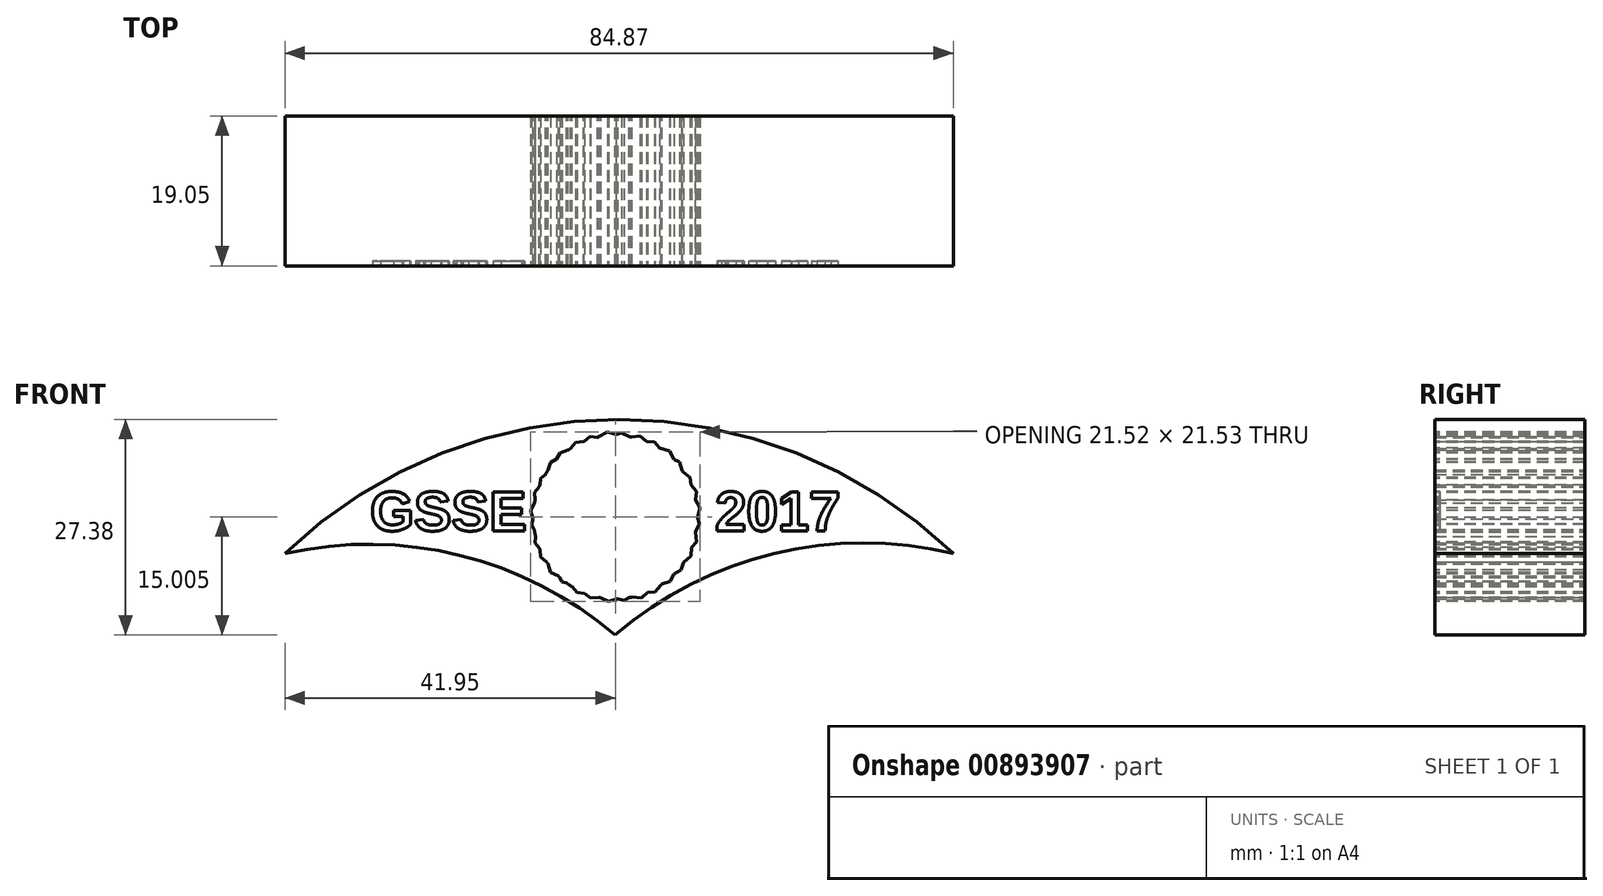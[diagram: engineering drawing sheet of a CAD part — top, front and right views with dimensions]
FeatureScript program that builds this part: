
annotation { "Feature Type Name" : "Feature", "Feature Type Description" : "" }
export const myFeature = defineFeature(function(context is Context, id is Id, definition is map)
    precondition{}
    {
        {
            var Q0;
            Q0=qCreatedBy(makeId("Front.planeOp"),FACE);
            var sketch = newSketch(context, id + "F0", { "sketchPlane" : qUnion([Q0])});
            skArc(sketch, "E0", {"start": v(0, 0) * mm, "mid": v(-19.73, 10.13) * mm, "end": v(-41.91, 10.32) * mm});
            skArc(sketch, "E1", {"start": v(42.96, 10.33) * mm, "mid": v(20.23, 10.36) * mm, "end": v(0, 0) * mm});
            skArc(sketch, "E2", {"start": v(42.96, 10.33) * mm, "mid": v(0.52, 27.38) * mm, "end": v(-41.91, 10.32) * mm});
            skCircle(sketch, "E3", {"center": v(0, 14.96) * mm, "radius": 10.39 * mm});
            skLineSegment(sketch, "E4", {"start": v(42.96, 10.33) * mm, "end": v(0, 10.33) * mm, "construction": true});
            skLineSegment(sketch, "E5", {"start": v(0, 10.33) * mm, "end": v(-41.91, 10.33) * mm, "construction": true});
            skLineSegment(sketch, "E6", {"start": v(10.39, 14.96) * mm, "end": v(-10.39, 14.96) * mm, "construction": true});
            skLineSegment(sketch, "E7", {"start": v(0, 0) * mm, "end": v(0, 27.38) * mm, "construction": true});
            skSolve(sketch);
        }
        {
            var Q0;
            Q0=makeQuery(id+"F0.imprint","IMPRINT",FACE,{"disambiguationData":[TD([[makeQuery(id+"F0.imprint","IMPRINT",EDGE,{"derivedFrom":sQuery(id+"F0.wireOp",EDGE,"E0")}),-1.0]])]});
            extrude(context, id + "F1", {"entities" : qUnion([Q0]), "depth" : 19.05 * mm, "offsetDistance" : 25.4 * mm});
        }
        {
            var Q0;
            Q0=makeQuery(id+"F1.opExtrude","CAP_FACE",FACE,{"disambiguationData":[OSD([sQuery(id+"F0.wireOp",EDGE,"E0"),sQuery(id+"F0.wireOp",EDGE,"E1"),sQuery(id+"F0.wireOp",EDGE,"E2"),sQuery(id+"F0.wireOp",EDGE,"E3")])],"isStart":false});
            var sketch = newSketch(context, id + "F2", { "sketchPlane" : qUnion([Q0])});
            skText(sketch, "E8", { "text": "GSSE", "fontName": "Arimo-Bold.ttf"});
            skLineSegment(sketch, "E9", {"start": v(-31.44, 18.39) * mm, "end": v(32.5, 18.39) * mm, "construction": true});
            skLineSegment(sketch, "E10", {"start": v(-38.65, 13.24) * mm, "end": v(39.7, 13.24) * mm, "construction": true});
            skLineSegment(sketch, "E11", {"start": v(0, 18.39) * mm, "end": v(0, 13.24) * mm, "construction": true});
            skLineSegment(sketch, "E12", {"start": v(-11, 15.81) * mm, "end": v(0, 15.81) * mm, "construction": true});
            skLineSegment(sketch, "E13", {"start": v(0, 15.81) * mm, "end": v(12.72, 16.05) * mm, "construction": true});
            skLineSegment(sketch, "E14", {"start": v(-31.11, 15.81) * mm, "end": v(-35.32, 15.81) * mm, "construction": true});
            skLineSegment(sketch, "E15", {"start": v(32.02, 15.33) * mm, "end": v(28.82, 15.33) * mm, "construction": true});
            skLineSegment(sketch, "E16", {"start": v(28.82, 18.39) * mm, "end": v(28.82, 13.24) * mm, "construction": true});
            skLineSegment(sketch, "E17", {"start": v(12.72, 18.39) * mm, "end": v(12.72, 13.24) * mm, "construction": true});
            skText(sketch, "E18", { "text": "2017", "fontName": "Arimo-Bold.ttf"});
            const initialGuessF2  = {"E8": [-0.03111, 0.01324, 1, 0, 0.00515], "E18": [0.01272, 0.01324, 1, 0, 0.00515]};
            skSetInitialGuess(sketch, initialGuessF2);
            skSolve(sketch);
        }
        {
            var Q0;
            Q0 = qSketchRegion(id + "F2", true);
            extrude(context, id + "F3", {"entities" : qUnion([Q0]), "operationType" : NewBodyOperationType.REMOVE, "oppositeDirection" : true, "depth" : 0.64 * mm, "offsetDistance" : 25.4 * mm});
        }
        {
            var Q0;
            {var subQ0=sQuery(id+"F0.wireOp",EDGE,"E1");var subQ1=sQuery(id+"F0.wireOp",EDGE,"E3");var subQ2=sQuery(id+"F0.wireOp",EDGE,"E0");var subQ3=sQuery(id+"F0.wireOp",EDGE,"E2");Q0=makeQuery(id+"F3.boolean.opBoolean","SPLIT",FACE,{"disambiguationData":[TD([makeQuery(id+"F1.opExtrude","SWEPT_FACE",FACE,{"disambiguationData":[OSD([subQ2])]})])],"derivedFrom":makeQuery(id+"F1.opExtrude","CAP_FACE",FACE,{"disambiguationData":[OSD([subQ2,subQ0,subQ3,subQ1])],"isStart":false})});}
            var sketch = newSketch(context, id + "F4", { "sketchPlane" : qUnion([Q0])});
            skCircle(sketch, "E19.cCircle", {"center": v(0, 14.96) * mm, "radius": 10.75 * mm, "construction": true});
            skLineSegment(sketch, "E19.0", {"start": v(6.99, 6.79) * mm, "end": v(-0.84, 4.24) * mm});
            skLineSegment(sketch, "E19.1", {"start": v(-0.84, 4.24) * mm, "end": v(-8.17, 7.97) * mm});
            skLineSegment(sketch, "E19.2", {"start": v(-8.17, 7.97) * mm, "end": v(-10.72, 15.8) * mm});
            skLineSegment(sketch, "E19.3", {"start": v(-10.72, 15.8) * mm, "end": v(-6.99, 23.14) * mm});
            skLineSegment(sketch, "E19.4", {"start": v(-6.99, 23.14) * mm, "end": v(0.84, 25.68) * mm});
            skLineSegment(sketch, "E19.5", {"start": v(0.84, 25.68) * mm, "end": v(8.17, 21.95) * mm});
            skLineSegment(sketch, "E19.6", {"start": v(8.17, 21.95) * mm, "end": v(10.72, 14.12) * mm});
            skLineSegment(sketch, "E19.7", {"start": v(10.72, 14.12) * mm, "end": v(6.99, 6.79) * mm});
            skLineSegment(sketch, "E20.0", {"start": v(3.36, 4.7) * mm, "end": v(-4.84, 5.38) * mm});
            skLineSegment(sketch, "E20.1", {"start": v(-4.84, 5.38) * mm, "end": v(-10.16, 11.67) * mm});
            skLineSegment(sketch, "E20.2", {"start": v(-10.16, 11.67) * mm, "end": v(-9.48, 19.87) * mm});
            skLineSegment(sketch, "E20.3", {"start": v(-9.48, 19.87) * mm, "end": v(-3.2, 25.19) * mm});
            skLineSegment(sketch, "E20.4", {"start": v(-3.2, 25.19) * mm, "end": v(5, 24.5) * mm});
            skLineSegment(sketch, "E20.5", {"start": v(5, 24.5) * mm, "end": v(10.32, 18.23) * mm});
            skLineSegment(sketch, "E20.6", {"start": v(10.32, 18.23) * mm, "end": v(9.64, 10.02) * mm});
            skLineSegment(sketch, "E20.7", {"start": v(9.64, 10.02) * mm, "end": v(3.36, 4.7) * mm});
            skLineSegment(sketch, "E21.0", {"start": v(5.1, 5.47) * mm, "end": v(-3.1, 4.68) * mm});
            skLineSegment(sketch, "E21.1", {"start": v(-3.1, 4.68) * mm, "end": v(-9.45, 9.9) * mm});
            skLineSegment(sketch, "E21.2", {"start": v(-9.45, 9.9) * mm, "end": v(-10.24, 18.1) * mm});
            skLineSegment(sketch, "E21.3", {"start": v(-10.24, 18.1) * mm, "end": v(-5, 24.46) * mm});
            skLineSegment(sketch, "E21.4", {"start": v(-5, 24.46) * mm, "end": v(3.19, 25.25) * mm});
            skLineSegment(sketch, "E21.5", {"start": v(3.19, 25.25) * mm, "end": v(9.54, 20.01) * mm});
            skLineSegment(sketch, "E21.6", {"start": v(9.54, 20.01) * mm, "end": v(10.33, 11.82) * mm});
            skLineSegment(sketch, "E21.7", {"start": v(10.33, 11.82) * mm, "end": v(5.1, 5.47) * mm});
            skLineSegment(sketch, "E22.0", {"start": v(1.13, 4.36) * mm, "end": v(-6.74, 6.76) * mm});
            skLineSegment(sketch, "E22.1", {"start": v(-6.74, 6.76) * mm, "end": v(-10.6, 14.03) * mm});
            skLineSegment(sketch, "E22.2", {"start": v(-10.6, 14.03) * mm, "end": v(-8.2, 21.9) * mm});
            skLineSegment(sketch, "E22.3", {"start": v(-8.2, 21.9) * mm, "end": v(-0.94, 25.77) * mm});
            skLineSegment(sketch, "E22.4", {"start": v(-0.94, 25.77) * mm, "end": v(6.93, 23.37) * mm});
            skLineSegment(sketch, "E22.5", {"start": v(6.93, 23.37) * mm, "end": v(10.8, 16.1) * mm});
            skLineSegment(sketch, "E22.6", {"start": v(10.8, 16.1) * mm, "end": v(8.4, 8.23) * mm});
            skLineSegment(sketch, "E22.7", {"start": v(8.4, 8.23) * mm, "end": v(1.13, 4.36) * mm});
            skSolve(sketch);
        }
        {
            var Q0;
            Q0 = qSketchRegion(id + "F4", true);
            extrude(context, id + "F5", {"entities" : qUnion([Q0]), "operationType" : NewBodyOperationType.REMOVE, "oppositeDirection" : true, "depth" : 25.4 * mm, "offsetDistance" : 25.4 * mm});
        }
    });
